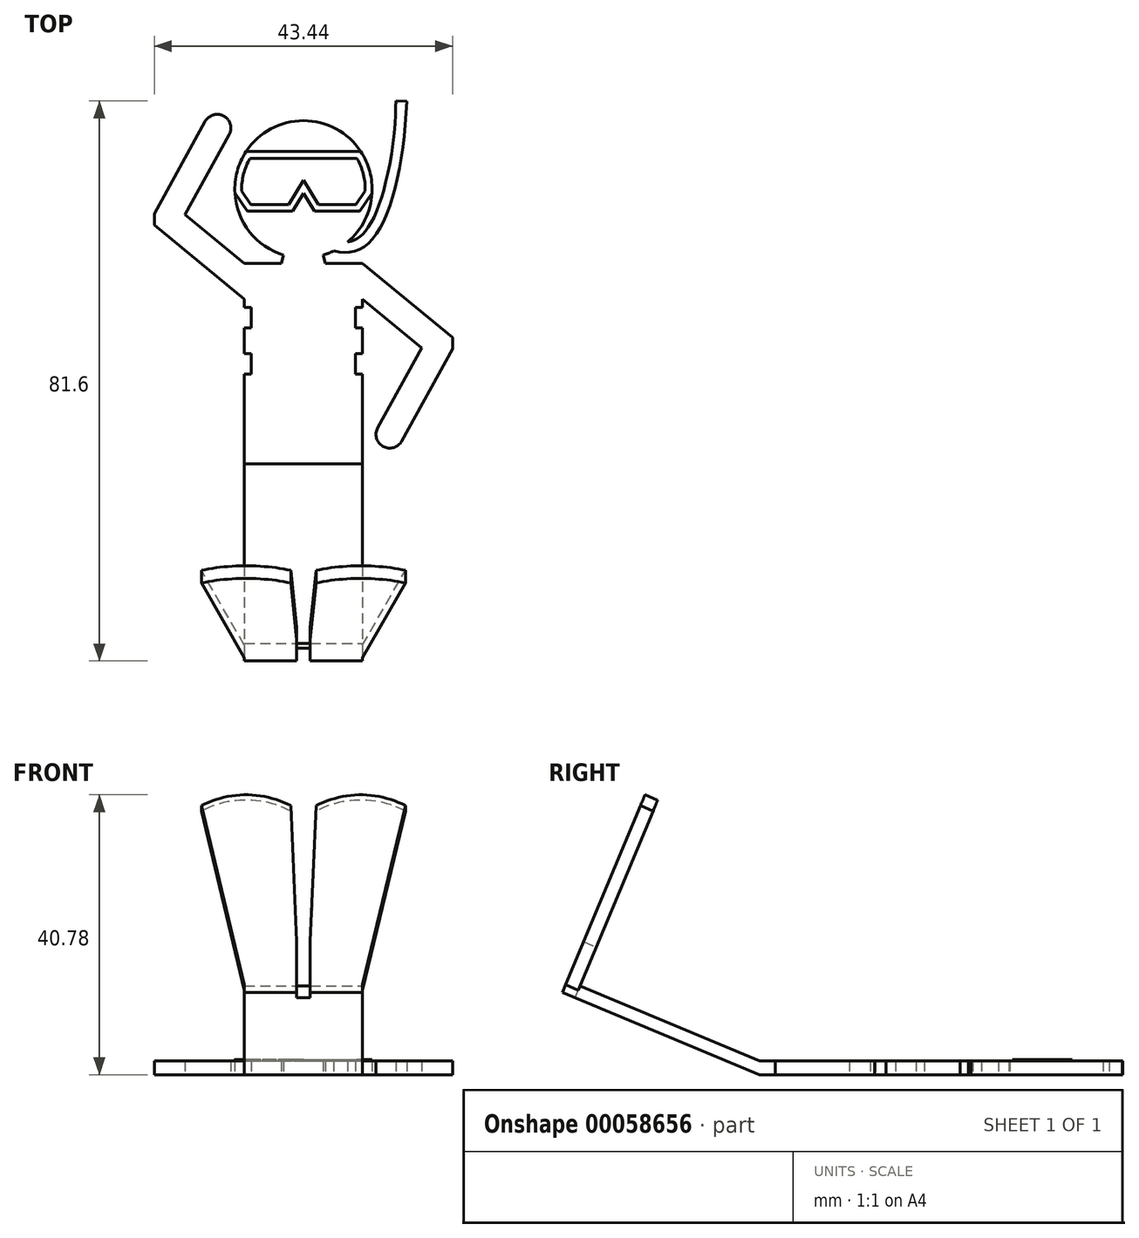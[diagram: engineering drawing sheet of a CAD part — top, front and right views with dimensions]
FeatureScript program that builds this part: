
annotation { "Feature Type Name" : "Feature", "Feature Type Description" : "" }
export const myFeature = defineFeature(function(context is Context, id is Id, definition is map)
    precondition{}
    {
        {
            var Q0;
            Q0=qCreatedBy(makeId("Top.planeOp"),FACE);
            var sketch = newSketch(context, id + "F0", { "sketchPlane" : qUnion([Q0])});
            skCircle(sketch, "E0", {"center": v(0, 0) * mm, "radius": 10 * mm});
            skLineSegment(sketch, "E1.rect.bottom", {"start": v(8.6, -40.02) * mm, "end": v(-8.6, -40.02) * mm});
            skLineSegment(sketch, "E1.rect.top", {"start": v(8.6, -10.8) * mm, "end": v(-8.6, -10.8) * mm});
            skLineSegment(sketch, "E1.rect.left", {"start": v(8.6, -40.02) * mm, "end": v(8.6, -26.91) * mm});
            skLineSegment(sketch, "E1.rect.right", {"start": v(-8.6, -40.02) * mm, "end": v(-8.6, -26.91) * mm});
            skPoint(sketch, "E1.rect.middle", {"position": v(0, -25.41) * mm});
            skLineSegment(sketch, "E2", {"start": v(-8.6, -10.8) * mm, "end": v(-21.71, -21.6) * mm});
            skLineSegment(sketch, "E3", {"start": v(-21.72, -23.25) * mm, "end": v(-14.32, -36.68) * mm});
            skLineSegment(sketch, "E4", {"start": v(-14.32, -36.68) * mm, "end": v(-10.81, -34.74) * mm});
            skLineSegment(sketch, "E5", {"start": v(-10.81, -34.74) * mm, "end": v(-17.23, -23.1) * mm});
            skLineSegment(sketch, "E6", {"start": v(-17.23, -23.1) * mm, "end": v(-8.6, -15.99) * mm});
            skLineSegment(sketch, "E7", {"start": v(0, 0) * mm, "end": v(0, 0) * mm});
            skPoint(sketch, "E7.endSnap0", {"position": v(0, -40.02) * mm});
            skLineSegment(sketch, "E8", {"start": v(0, 0) * mm, "end": v(-3.24, -10.8) * mm});
            skLineSegment(sketch, "E9.MirrorCS", {"start": v(0, 0) * mm, "end": v(3.2, -10.81) * mm});
            skLineSegment(sketch, "E10", {"start": v(-21.71, -21.6) * mm, "end": v(-21.72, -23.25) * mm});
            skFitSpline(sketch, "E11", {"points": [v(-0.01, -7.03) * mm, v(8.6, -8.54) * mm, v(15.04, 12.8) * mm], "startDerivative": vector(24.74, -13.93) * mm, "endDerivative": vector(1.92, 48.5) * mm});
            skFitSpline(sketch, "E12.0", {"points": [v(0.75, -5.68) * mm, v(1.25, -5.96) * mm, v(2.23, -6.48) * mm, v(3.6, -7.1) * mm, v(4.87, -7.5) * mm, v(5.97, -7.68) * mm, v(6.74, -7.62) * mm, v(7.28, -7.47) * mm, v(7.67, -7.3) * mm, v(8.05, -7.05) * mm, v(8.46, -6.7) * mm, v(8.88, -6.25) * mm, v(9.44, -5.51) * mm, v(10.13, -4.34) * mm, v(10.89, -2.58) * mm, v(11.57, -0.52) * mm, v(12.36, 2.58) * mm, v(13.1, 7) * mm, v(13.4, 10.89) * mm, v(13.48, 12.87) * mm]});
            skLineSegment(sketch, "E13", {"start": v(13.48, 12.87) * mm, "end": v(15.04, 12.8) * mm});
            skLineSegment(sketch, "E14.rect.bottom", {"start": v(-7.6, -26.91) * mm, "end": v(-8.6, -26.91) * mm});
            skLineSegment(sketch, "E14.rect.top", {"start": v(-7.6, -23.91) * mm, "end": v(-8.6, -23.91) * mm});
            skLineSegment(sketch, "E14.rect.left", {"start": v(-7.6, -26.91) * mm, "end": v(-7.6, -23.91) * mm});
            skPoint(sketch, "E14.rect.middle", {"position": v(-8.6, -25.41) * mm});
            skPoint(sketch, "E15.orphan", {"position": v(-9.6, -26.91) * mm});
            skLineSegment(sketch, "E16", {"start": v(0, -40.72) * mm, "end": v(0, -25.41) * mm, "construction": true});
            skLineSegment(sketch, "E17.MirrorCS", {"start": v(7.6, -23.91) * mm, "end": v(8.6, -23.91) * mm});
            skLineSegment(sketch, "E18.MirrorCS", {"start": v(7.6, -26.91) * mm, "end": v(7.6, -23.91) * mm});
            skLineSegment(sketch, "E19.MirrorCS", {"start": v(7.6, -26.91) * mm, "end": v(8.6, -26.91) * mm});
            skLineSegment(sketch, "E20.trimOffspring", {"start": v(-8.6, -23.91) * mm, "end": v(-8.6, -20.21) * mm});
            skLineSegment(sketch, "E21.trimOffspring", {"start": v(8.6, -23.91) * mm, "end": v(8.6, -20.21) * mm});
            skLineSegment(sketch, "E22", {"start": v(-8.6, -22.06) * mm, "end": v(8.6, -22.06) * mm, "construction": true});
            skLineSegment(sketch, "E23.MirrorCS", {"start": v(-7.6, -20.21) * mm, "end": v(-8.6, -20.21) * mm});
            skLineSegment(sketch, "E24.MirrorCS", {"start": v(-7.6, -17.21) * mm, "end": v(-7.6, -20.21) * mm});
            skLineSegment(sketch, "E25.MirrorCS", {"start": v(-7.6, -17.21) * mm, "end": v(-8.6, -17.21) * mm});
            skLineSegment(sketch, "E26.MirrorCS", {"start": v(7.6, -20.21) * mm, "end": v(8.6, -20.21) * mm});
            skLineSegment(sketch, "E27.MirrorCS", {"start": v(7.6, -17.21) * mm, "end": v(7.6, -20.21) * mm});
            skLineSegment(sketch, "E28.MirrorCS", {"start": v(7.6, -17.21) * mm, "end": v(8.6, -17.21) * mm});
            skLineSegment(sketch, "E29.trimOffspring", {"start": v(8.6, -17.21) * mm, "end": v(8.6, -10.8) * mm});
            skLineSegment(sketch, "E30.trimOffspring", {"start": v(-8.6, -17.21) * mm, "end": v(-8.6, -10.8) * mm});
            skArc(sketch, "E31", {"start": v(-14.32, -36.68) * mm, "mid": v(-11.6, -37.46) * mm, "end": v(-10.81, -34.74) * mm});
            skLineSegment(sketch, "E32.MirrorCS", {"start": v(8.6, -10.8) * mm, "end": v(21.71, -21.6) * mm});
            skLineSegment(sketch, "E33.MirrorCS", {"start": v(17.23, -23.1) * mm, "end": v(8.6, -15.99) * mm});
            skLineSegment(sketch, "E34.MirrorCS", {"start": v(21.71, -21.6) * mm, "end": v(21.72, -23.25) * mm});
            skLineSegment(sketch, "E35.MirrorCS", {"start": v(10.81, -34.74) * mm, "end": v(17.23, -23.1) * mm});
            skLineSegment(sketch, "E36.MirrorCS", {"start": v(21.72, -23.25) * mm, "end": v(14.32, -36.68) * mm});
            skArc(sketch, "E37.MirrorCS", {"start": v(14.32, -36.68) * mm, "mid": v(11.6, -37.46) * mm, "end": v(10.81, -34.74) * mm});
            skLineSegment(sketch, "E38", {"start": v(-8.6, -15.99) * mm, "end": v(-8.6, -10.8) * mm});
            skLineSegment(sketch, "E39", {"start": v(-8.6, -13.4) * mm, "end": v(8.6, -13.4) * mm, "construction": true});
            skLineSegment(sketch, "E40.MirrorCS", {"start": v(-8.6, -15.99) * mm, "end": v(-21.71, -5.19) * mm});
            skLineSegment(sketch, "E41.MirrorCS", {"start": v(-17.23, -3.7) * mm, "end": v(-8.6, -10.8) * mm});
            skLineSegment(sketch, "E42.MirrorCS", {"start": v(-21.71, -5.19) * mm, "end": v(-21.72, -3.54) * mm});
            skLineSegment(sketch, "E43.MirrorCS", {"start": v(-21.72, -3.54) * mm, "end": v(-14.32, 9.88) * mm});
            skLineSegment(sketch, "E44.MirrorCS", {"start": v(-10.81, 7.95) * mm, "end": v(-17.23, -3.7) * mm});
            skArc(sketch, "E45.MirrorCS", {"start": v(-14.32, 9.88) * mm, "mid": v(-11.6, 10.67) * mm, "end": v(-10.81, 7.95) * mm});
            skSolve(sketch);
        }
        {
            var Q0;
            {var subQ5=sQuery(id+"F0.wireOp",EDGE,"E13");Q0=makeQuery(id+"F0.imprint","IMPRINT",FACE,{"disambiguationData":[TD([[makeQuery(id+"F0.imprint","IMPRINT",EDGE,{"derivedFrom":subQ5}),-1.0]])]});}
            var Q1;
            {var subQ0=sQuery(id+"F0.wireOp",EDGE,"E9.MirrorCS");var subQ1=sQuery(id+"F0.wireOp",EDGE,"E0");var subQ2=makeQuery(id+"F0.imprint","INTERSECT",VERTEX,{"derivedFrom":[subQ1,subQ0]});Q1=makeQuery(id+"F0.imprint","IMPRINT",FACE,{"disambiguationData":[TD([[makeQuery(id+"F0.imprint","IMPRINT",EDGE,{"disambiguationData":[TD([[subQ2,1.0]])],"derivedFrom":subQ1}),-1.0]])]});}
            var Q2;
            {var subQ0=sQuery(id+"F0.wireOp",EDGE,"E9.MirrorCS");var subQ1=sQuery(id+"F0.wireOp",EDGE,"E0");var subQ2=makeQuery(id+"F0.imprint","INTERSECT",VERTEX,{"derivedFrom":[subQ1,subQ0]});Q2=makeQuery(id+"F0.imprint","IMPRINT",FACE,{"disambiguationData":[TD([[makeQuery(id+"F0.imprint","IMPRINT",EDGE,{"disambiguationData":[TD([[subQ2,-1.0]])],"derivedFrom":subQ1}),1.0]])]});}
            var Q3;
            {var subQ0=sQuery(id+"F0.wireOp",EDGE,"E8");var subQ1=sQuery(id+"F0.wireOp",EDGE,"E0");var subQ2=makeQuery(id+"F0.imprint","INTERSECT",VERTEX,{"derivedFrom":[subQ1,subQ0]});Q3=makeQuery(id+"F0.imprint","IMPRINT",FACE,{"disambiguationData":[TD([[makeQuery(id+"F0.imprint","IMPRINT",EDGE,{"disambiguationData":[TD([[subQ2,1.0]])],"derivedFrom":subQ1}),1.0]])]});}
            var Q4;
            {var subQ0=sQuery(id+"F0.wireOp",EDGE,"E2");Q4=makeQuery(id+"F0.imprint","IMPRINT",FACE,{"disambiguationData":[TD([[makeQuery(id+"F0.imprint","IMPRINT",EDGE,{"derivedFrom":subQ0}),1.0]])]});}
            var Q5;
            Q5=makeQuery(id+"F0.imprint","IMPRINT",FACE,{"disambiguationData":[TD([[makeQuery(id+"F0.imprint","IMPRINT",EDGE,{"derivedFrom":sQuery(id+"F0.wireOp",EDGE,"E1.rect.bottom")}),-1.0]])]});
            var Q6;
            {var subQ0=sQuery(id+"F0.wireOp",EDGE,"E9.MirrorCS");var subQ5=sQuery(id+"F0.wireOp",EDGE,"E0");var subQ7=makeQuery(id+"F0.imprint","INTERSECT",VERTEX,{"derivedFrom":[subQ5,subQ0]});Q6=makeQuery(id+"F0.imprint","IMPRINT",FACE,{"disambiguationData":[TD([[makeQuery(id+"F0.imprint","IMPRINT",EDGE,{"disambiguationData":[TD([[subQ7,1.0]])],"derivedFrom":subQ5}),1.0]])]});}
            var Q7;
            {var subQ0=sQuery(id+"F0.wireOp",EDGE,"E11");var subQ1=sQuery(id+"F0.wireOp",EDGE,"E0");var subQ2=makeQuery(id+"F0.imprint","INTERSECT",VERTEX,{"derivedFrom":[subQ1,subQ0]});Q7=makeQuery(id+"F0.imprint","IMPRINT",FACE,{"disambiguationData":[TD([[makeQuery(id+"F0.imprint","IMPRINT",EDGE,{"disambiguationData":[TD([[subQ2,-1.0]])],"derivedFrom":subQ1}),1.0]])]});}
            var Q8;
            {var subQ1=sQuery(id+"F0.wireOp",EDGE,"52ec6f5b-0911-45c1-9ac7-03cc07f0d4f40.MirrorCS");Q8=makeQuery(id+"F0.imprint","IMPRINT",FACE,{"disambiguationData":[TD([[makeQuery(id+"F0.imprint","IMPRINT",EDGE,{"derivedFrom":subQ1}),-1.0]])]});}
            var Q9;
            {var subQ1=sQuery(id+"F0.wireOp",EDGE,"E32.MirrorCS");Q9=makeQuery(id+"F0.imprint","IMPRINT",FACE,{"disambiguationData":[TD([[makeQuery(id+"F0.imprint","IMPRINT",EDGE,{"derivedFrom":subQ1}),-1.0]])]});}
            var Q10;
            {var subQ0=sQuery(id+"F0.wireOp",EDGE,"E41.MirrorCS");Q10=makeQuery(id+"F0.imprint","IMPRINT",FACE,{"disambiguationData":[TD([[makeQuery(id+"F0.imprint","IMPRINT",EDGE,{"derivedFrom":subQ0}),-1.0]])]});}
            extrude(context, id + "F1", {"entities" : qUnion([Q0, Q1, Q2, Q3, Q4, Q5, Q6, Q7, Q8, Q9, Q10]), "depth" : 2 * mm});
        }
        {
            var Q0;
            {var subQ0=sQuery(id+"F0.wireOp",EDGE,"E1.rect.left");Q0=makeQuery(id+"F1.opExtrude","SWEPT_FACE",FACE,{"disambiguationData":[OSD([subQ0]),TDD([makeQuery(id+"F0.imprint","IMPRINT",EDGE,{"disambiguationData":[TD([[makeQuery(id+"F0.imprint","INTERSECT",VERTEX,{"derivedFrom":[sQuery(id+"F0.wireOp",EDGE,"E1.rect.bottom"),subQ0]}),-1.0]])],"derivedFrom":subQ0})])]});}
            var sketch = newSketch(context, id + "F2", { "sketchPlane" : qUnion([Q0])});
            skLineSegment(sketch, "E46", {"start": v(-40.02, 2) * mm, "end": v(-68.73, 14) * mm});
            skLineSegment(sketch, "E47", {"start": v(-40.02, 0) * mm, "end": v(-68.73, 12) * mm});
            skLineSegment(sketch, "E48", {"start": v(-68.73, 12) * mm, "end": v(-68.73, 14) * mm});
            skLineSegment(sketch, "E49", {"start": v(-68.73, 12) * mm, "end": v(-65.65, 19.38) * mm});
            skLineSegment(sketch, "E50", {"start": v(-65.65, 19.38) * mm, "end": v(-63.8, 18.6) * mm});
            skLineSegment(sketch, "E51", {"start": v(-63.8, 18.6) * mm, "end": v(-66.89, 11.23) * mm});
            skSolve(sketch);
        }
        {
            var Q0;
            Q0=makeQuery(id+"F2.imprint","IMPRINT",FACE,{"disambiguationData":[TD([[makeQuery(id+"F2.imprint","IMPRINT",EDGE,{"derivedFrom":sQuery(id+"F2.wireOp",EDGE,"E47")}),-1.0]])]});
            var Q1;
            {var subQ0=sQuery(id+"F2.wireOp",EDGE,"n6M02J3H-BiTj-s5m4-DXqR-OacXoYUZd4Ws");Q1=makeQuery(id+"F2.imprint","IMPRINT",FACE,{"disambiguationData":[TD([[makeQuery(id+"F2.imprint","IMPRINT",EDGE,{"derivedFrom":subQ0}),-1.0]])]});}
            var Q2;
            {var subQ5=sQuery(id+"F2.wireOp",EDGE,"E50");Q2=makeQuery(id+"F2.imprint","IMPRINT",FACE,{"disambiguationData":[TD([[makeQuery(id+"F2.imprint","IMPRINT",EDGE,{"derivedFrom":subQ5}),-1.0]])]});}
            var Q3;
            Q3=makeQuery(id+"F1.opExtrude","SWEPT_FACE",FACE,{"disambiguationData":[OSD([sQuery(id+"F0.wireOp",EDGE,"E1.rect.right")])]});
            extrude(context, id + "F3", {"entities" : qUnion([Q0, Q1, Q2]), "operationType" : NewBodyOperationType.ADD, "endBound" : BoundingType.UP_TO_SURFACE, "oppositeDirection" : true, "endBoundEntityFace" : qUnion([Q3]), "depth" : 25 * mm});
        }
        {
            var Q0;
            Q0=makeQuery(id+"F3.opExtrude","SWEPT_FACE",FACE,{"disambiguationData":[OSD([sQuery(id+"F2.wireOp",EDGE,"E50")])]});
            var sketch = newSketch(context, id + "F4", { "sketchPlane" : qUnion([Q0])});
            skLineSegment(sketch, "E52", {"start": v(0, -69.76) * mm, "end": v(0, -44.76) * mm});
            skPoint(sketch, "E52.endSnap0", {"position": v(0, -67.28) * mm});
            skArc(sketch, "E53.0.startCap", {"start": v(1, -69.76) * mm, "mid": v(0, -70.76) * mm, "end": v(-1, -69.76) * mm});
            skArc(sketch, "E53.0.endCap", {"start": v(-1, -44.76) * mm, "mid": v(0, -43.76) * mm, "end": v(1, -44.76) * mm});
            skLineSegment(sketch, "E53.0.left", {"start": v(-1, -69.76) * mm, "end": v(-1, -44.76) * mm});
            skLineSegment(sketch, "E53.0.right", {"start": v(1, -69.76) * mm, "end": v(1, -44.76) * mm});
            skSolve(sketch);
        }
        {
            var Q0;
            {var subQ5=sQuery(id+"F4.wireOp",EDGE,"E53.0.endCap");Q0=makeQuery(id+"F4.imprint","IMPRINT",FACE,{"disambiguationData":[TD([[makeQuery(id+"F4.imprint","IMPRINT",EDGE,{"derivedFrom":subQ5}),-1.0]])]});}
            var Q1;
            {var subQ0=sQuery(id+"F4.wireOp",EDGE,"E52");var subQ1=sQuery(id+"F2.wireOp",EDGE,"IUaCcnN7-Gwlh-9XYi-XDCx-exDYD3MmbBha");var subQ2=makeQuery(id+"F3.opExtrude","SWEPT_EDGE",EDGE,{"disambiguationData":[OSD([sQuery(id+"F2.wireOp",EDGE,"n6M02J3H-BiTj-s5m4-DXqR-OacXoYUZd4Ws"),subQ1])]});var subQ3=makeQuery(id+"F4.imprint","INTERSECT",VERTEX,{"derivedFrom":[subQ2,subQ0]});Q1=makeQuery(id+"F4.imprint","IMPRINT",FACE,{"disambiguationData":[TD([[makeQuery(id+"F4.imprint","IMPRINT",EDGE,{"disambiguationData":[TD([[subQ3,-1.0]])],"derivedFrom":subQ0}),-1.0]])]});}
            var Q2;
            {var subQ0=sQuery(id+"F4.wireOp",EDGE,"E52");var subQ1=sQuery(id+"F2.wireOp",EDGE,"IUaCcnN7-Gwlh-9XYi-XDCx-exDYD3MmbBha");var subQ2=makeQuery(id+"F3.opExtrude","SWEPT_EDGE",EDGE,{"disambiguationData":[OSD([sQuery(id+"F2.wireOp",EDGE,"n6M02J3H-BiTj-s5m4-DXqR-OacXoYUZd4Ws"),subQ1])]});var subQ3=makeQuery(id+"F4.imprint","INTERSECT",VERTEX,{"derivedFrom":[subQ2,subQ0]});Q2=makeQuery(id+"F4.imprint","IMPRINT",FACE,{"disambiguationData":[TD([[makeQuery(id+"F4.imprint","IMPRINT",EDGE,{"disambiguationData":[TD([[subQ3,-1.0]])],"derivedFrom":subQ0}),1.0]])]});}
            var Q3;
            {var subQ0=sQuery(id+"F4.wireOp",EDGE,"E53.0.startCap");Q3=makeQuery(id+"F4.imprint","IMPRINT",FACE,{"disambiguationData":[TD([[makeQuery(id+"F4.imprint","IMPRINT",EDGE,{"derivedFrom":subQ0}),-1.0]])]});}
            extrude(context, id + "F5", {"entities" : qUnion([Q0, Q1, Q2, Q3]), "operationType" : NewBodyOperationType.REMOVE, "oppositeDirection" : true, "depth" : 25 * mm});
        }
        {
            var Q0;
            {var subQ2=sQuery(id+"F2.wireOp",EDGE,"E49");Q0=makeQuery(id+"F5.boolean.opBoolean","SPLIT",FACE,{"disambiguationData":[TD([makeQuery(id+"F1.opExtrude","SWEPT_FACE",FACE,{"disambiguationData":[OSD([sQuery(id+"F0.wireOp",EDGE,"E1.rect.right")])]})])],"derivedFrom":makeQuery(id+"F3.opExtrude","SWEPT_FACE",FACE,{"disambiguationData":[OSD([subQ2])]})});}
            var sketch = newSketch(context, id + "F6", { "sketchPlane" : qUnion([Q0])});
            skLineSegment(sketch, "E54.0.0", {"start": v(-1, -15.43) * mm, "end": v(-1, -7.43) * mm});
            skLineSegment(sketch, "E54.0.1", {"start": v(-1, -7.43) * mm, "end": v(-8.6, -7.43) * mm, "construction": true});
            skLineSegment(sketch, "E54.0.2", {"start": v(-8.6, -15.43) * mm, "end": v(-8.6, -15.43) * mm});
            skLineSegment(sketch, "E54.0.3", {"start": v(-8.6, -15.43) * mm, "end": v(-1, -15.43) * mm});
            skLineSegment(sketch, "E55.0.0", {"start": v(8.6, -7.43) * mm, "end": v(1, -7.43) * mm, "construction": true});
            skLineSegment(sketch, "E55.0.1", {"start": v(1, -7.43) * mm, "end": v(1, -15.43) * mm, "construction": true});
            skLineSegment(sketch, "E55.0.2", {"start": v(1, -15.43) * mm, "end": v(8.6, -15.43) * mm, "construction": true});
            skLineSegment(sketch, "E55.0.3", {"start": v(8.6, -15.43) * mm, "end": v(8.6, -7.43) * mm, "construction": true});
            skLineSegment(sketch, "E56", {"start": v(-14.87, 14.04) * mm, "end": v(-1.85, 14.04) * mm});
            skLineSegment(sketch, "E57", {"start": v(-1.85, 14.04) * mm, "end": v(-1, -7.43) * mm});
            skArc(sketch, "E58", {"start": v(-1.85, 14.04) * mm, "mid": v(-8.36, 15.76) * mm, "end": v(-14.87, 14.04) * mm});
            skLineSegment(sketch, "E59", {"start": v(0, 0) * mm, "end": v(0, -28.06) * mm, "construction": true});
            skLineSegment(sketch, "E60.MirrorCS", {"start": v(8.6, -15.43) * mm, "end": v(1, -15.43) * mm});
            skLineSegment(sketch, "E61.MirrorCS", {"start": v(1, -15.43) * mm, "end": v(1, -7.43) * mm});
            skArc(sketch, "E62.MirrorCS", {"start": v(1.85, 14.04) * mm, "mid": v(8.36, 15.76) * mm, "end": v(14.87, 14.04) * mm});
            skLineSegment(sketch, "E63.MirrorCS", {"start": v(1.85, 14.04) * mm, "end": v(1, -7.43) * mm});
            skLineSegment(sketch, "E64", {"start": v(-8.6, -14.25) * mm, "end": v(-14.87, 14.04) * mm});
            skLineSegment(sketch, "E65.MirrorCS", {"start": v(8.6, -14.25) * mm, "end": v(14.87, 14.04) * mm});
            skLineSegment(sketch, "E66.0.0", {"start": v(8.6, -7.43) * mm, "end": v(1, -7.43) * mm});
            skLineSegment(sketch, "E66.0.1", {"start": v(1, -7.43) * mm, "end": v(1, -15.43) * mm});
            skLineSegment(sketch, "E66.0.2", {"start": v(1, -15.43) * mm, "end": v(8.6, -15.43) * mm});
            skLineSegment(sketch, "E66.0.3", {"start": v(8.6, -15.43) * mm, "end": v(8.6, -7.43) * mm});
            skSolve(sketch);
        }
        {
            var Q0;
            Q0 = qSketchRegion(id + "F6", true);
            var Q1;
            Q1=makeQuery(id+"F6.imprint","IMPRINT",FACE,{"disambiguationData":[TD([[makeQuery(id+"F6.imprint","IMPRINT",EDGE,{"derivedFrom":sQuery(id+"F6.wireOp",EDGE,"E56")}),-1.0]])]});
            extrude(context, id + "F7", {"entities" : qUnion([Q0, Q1]), "operationType" : NewBodyOperationType.ADD, "oppositeDirection" : true, "depth" : 2 * mm});
        }
        {
            var Q0;
            Q0=makeQuery(id+"F1.opExtrude","CAP_FACE",FACE,{"disambiguationData":[OSD([sQuery(id+"F0.wireOp",EDGE,"E0"),sQuery(id+"F0.wireOp",EDGE,"E1.rect.bottom"),sQuery(id+"F0.wireOp",EDGE,"E1.rect.top"),sQuery(id+"F0.wireOp",EDGE,"E1.rect.left"),sQuery(id+"F0.wireOp",EDGE,"E1.rect.right"),sQuery(id+"F0.wireOp",EDGE,"E2"),sQuery(id+"F0.wireOp",EDGE,"E3"),sQuery(id+"F0.wireOp",EDGE,"E4"),sQuery(id+"F0.wireOp",EDGE,"E5"),sQuery(id+"F0.wireOp",EDGE,"E6"),sQuery(id+"F0.wireOp",EDGE,"a1109bb8-16db-48b2-8a0d-a93e20861b760.MirrorCS"),sQuery(id+"F0.wireOp",EDGE,"4f4e385c-b6b2-4004-b51a-c9fdc2b669e70.MirrorCS"),sQuery(id+"F0.wireOp",EDGE,"52ec6f5b-0911-45c1-9ac7-03cc07f0d4f40.MirrorCS"),sQuery(id+"F0.wireOp",EDGE,"05866ef2-5ad8-488a-ac46-24d70ad5c9000.MirrorCS"),sQuery(id+"F0.wireOp",EDGE,"52a41d33-9d39-4bfe-b236-42e17a3f4df00.MirrorCS"),sQuery(id+"F0.wireOp",EDGE,"E8"),sQuery(id+"F0.wireOp",EDGE,"E9.MirrorCS"),sQuery(id+"F0.wireOp",EDGE,"E10"),sQuery(id+"F0.wireOp",EDGE,"63791d01-9245-4826-917b-9e75567109cc0.MirrorCS"),sQuery(id+"F0.wireOp",EDGE,"E11"),sQuery(id+"F0.wireOp",EDGE,"E12.0"),sQuery(id+"F0.wireOp",EDGE,"E13"),sQuery(id+"F0.wireOp",EDGE,"E14.rect.bottom"),sQuery(id+"F0.wireOp",EDGE,"E14.rect.top"),sQuery(id+"F0.wireOp",EDGE,"E14.rect.left"),sQuery(id+"F0.wireOp",EDGE,"E17.MirrorCS"),sQuery(id+"F0.wireOp",EDGE,"E18.MirrorCS"),sQuery(id+"F0.wireOp",EDGE,"E19.MirrorCS"),sQuery(id+"F0.wireOp",EDGE,"E20.trimOffspring"),sQuery(id+"F0.wireOp",EDGE,"E21.trimOffspring"),sQuery(id+"F0.wireOp",EDGE,"E23.MirrorCS"),sQuery(id+"F0.wireOp",EDGE,"E24.MirrorCS"),sQuery(id+"F0.wireOp",EDGE,"E25.MirrorCS"),sQuery(id+"F0.wireOp",EDGE,"E26.MirrorCS"),sQuery(id+"F0.wireOp",EDGE,"E27.MirrorCS"),sQuery(id+"F0.wireOp",EDGE,"E28.MirrorCS"),sQuery(id+"F0.wireOp",EDGE,"E29.trimOffspring"),sQuery(id+"F0.wireOp",EDGE,"E30.trimOffspring")])],"isStart":false});
            var sketch = newSketch(context, id + "F8", { "sketchPlane" : qUnion([Q0])});
            skArc(sketch, "E67.0", {"start": v(6.46, -7.63) * mm, "mid": v(9.9, -1.41) * mm, "end": v(8.34, 5.52) * mm, "construction": true});
            skLineSegment(sketch, "E68", {"start": v(-8.34, 5.52) * mm, "end": v(8.34, 5.52) * mm});
            skLineSegment(sketch, "E69", {"start": v(0, -0.58) * mm, "end": v(-1.59, -3.2) * mm});
            skLineSegment(sketch, "E70", {"start": v(-1.59, -3.2) * mm, "end": v(-8.18, -3.2) * mm});
            skLineSegment(sketch, "E71", {"start": v(-8.18, -3.2) * mm, "end": v(-9.98, -0.58) * mm});
            skLineSegment(sketch, "E72", {"start": v(0, 7.77) * mm, "end": v(0, -9.39) * mm, "construction": true});
            skArc(sketch, "E73.trimOffspring", {"start": v(-8.34, 5.52) * mm, "mid": v(-9.65, 2.6) * mm, "end": v(-9.98, -0.58) * mm, "construction": true});
            skPoint(sketch, "E74.orphan", {"position": v(-2.87, -9.58) * mm});
            skLineSegment(sketch, "E75.MirrorCS", {"start": v(0, -0.58) * mm, "end": v(1.59, -3.2) * mm});
            skLineSegment(sketch, "E76.MirrorCS", {"start": v(1.59, -3.2) * mm, "end": v(8.18, -3.2) * mm});
            skLineSegment(sketch, "E77.MirrorCS", {"start": v(8.18, -3.2) * mm, "end": v(9.98, -0.58) * mm});
            skArc(sketch, "E78.MirrorCS", {"start": v(8.34, 5.52) * mm, "mid": v(9.65, 2.6) * mm, "end": v(9.98, -0.58) * mm, "construction": true});
            skArc(sketch, "E79.0", {"start": v(-7.78, 4.52) * mm, "mid": v(-8.72, 2.22) * mm, "end": v(-9, -0.25) * mm});
            skLineSegment(sketch, "E79.1", {"start": v(-7.66, -2.2) * mm, "end": v(-9, -0.25) * mm});
            skLineSegment(sketch, "E79.2", {"start": v(-7.78, 4.52) * mm, "end": v(7.78, 4.52) * mm});
            skLineSegment(sketch, "E79.3", {"start": v(-2.15, -2.2) * mm, "end": v(-7.66, -2.2) * mm});
            skLineSegment(sketch, "E79.4", {"start": v(0, 1.36) * mm, "end": v(-2.15, -2.2) * mm});
            skArc(sketch, "E79.5", {"start": v(7.78, 4.52) * mm, "mid": v(8.72, 2.22) * mm, "end": v(9, -0.25) * mm});
            skLineSegment(sketch, "E79.6", {"start": v(7.66, -2.2) * mm, "end": v(9, -0.25) * mm});
            skLineSegment(sketch, "E79.7", {"start": v(2.15, -2.2) * mm, "end": v(7.66, -2.2) * mm});
            skLineSegment(sketch, "E79.8", {"start": v(0, 1.36) * mm, "end": v(2.15, -2.2) * mm});
            skSolve(sketch);
        }
        {
            var Q0;
            {var subQ1=sQuery(id+"F8.wireOp",EDGE,"E68");Q0=makeQuery(id+"F8.imprint","IMPRINT",FACE,{"disambiguationData":[TD([[makeQuery(id+"F8.imprint","IMPRINT",EDGE,{"derivedFrom":subQ1}),-1.0]])]});}
            extrude(context, id + "F9", {"entities" : qUnion([Q0]), "operationType" : NewBodyOperationType.ADD, "depth" : .2 * mm});
        }
    });
